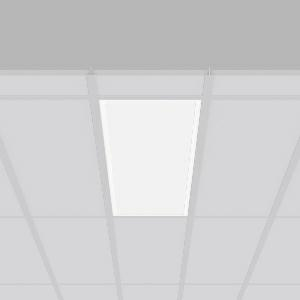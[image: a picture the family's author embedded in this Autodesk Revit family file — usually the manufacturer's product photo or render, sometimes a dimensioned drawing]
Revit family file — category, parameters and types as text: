
# Revit family: sidelite_eco_672372_002_04_a6ed
name_source: partatom
category: Lighting Fixtures
units: mm (PartAtom-declared; Revit-internal decimal feet)

## family parameters
Cut with Voids When Loaded = No
Host = Face
Light Source = No
Part Type = Normal
Room Calculation Point = No
Round Connector Dimension = Use Diameter
Shared = No

## types (1)
- SIDELITE ECO (1 x LED Modul 830, 3300 lm, 3000)
    Apparent Load = 29 VA
    CIE Flux Codes = 46 79 96 100 100
    Color Rendering = 80
    Color Temperature = 3000
    Default Elevation = 1800 mm
    Description = Series: SIDELITE ECO
Highly economical recessed luminaire with progressive LED technology. For escape route illumination. Frame made of aluminium, powder-coated. Diffuser: plastic, opal. Lightguide and diffuser made of non-yellowing plastic (PMMA). Lateral light emission (RZB SIDELITE technology) for homogeneous light distribution. External driver. Self-contained system with automatic self-test and feedback to the RZB monitoring system MULTIDIGIT. External driver with simple plug-in locking system. Extended connection cable (1.90 m). 
Colour: white
Length: 1195 mm
Width: 295 mm
Cut-out length: 1170 mm
Cut-out width: 270 mm
Recess height: 160 mm
Luminaire: recess height: 40 mm
Weight: 4.4 kg
Operating mode: maintained power mode
Duration time: 8 h
Lamp: LED
Socket: without socket
Colour temperature: 3000K
Colour rendering index (CRI): 80
System power: 29 W
Rated luminous flux: 3300 lm
Luminous flux, emergency: 220 lm
System power, emergency: 0.1 W
Control gear: Regulated power supply
Protection class: I
Type of protection: IP 40
    Height = 0 mm  [stored 0 ft]
    Lamp = 1 x LED Modul 830
    Lamp Light Flux = 3300 lm
    Lamp count = 1
    Length = 1195 mm
    Lifetime = 50000 h
    Luminous efficacy = 114 lm/W
    Manufacturer = RZB
    ModVariant = No
    Model = 672372.002.04
    Mounting Place = Ceiling
    Mounting Type = Recessed
    Number of Poles = 1
    OnlyDefault = Yes
    Power Factor = 1
    Product Name = SIDELITE ECO
    Product group = Recessed modular luminaires
    ProductGroupID = 406
    Protection Class = Protection class I
    Protection Degree = IP 40
    RLX_Detail_Level = 1
    RLX_Emergency_Light_Flux = 220 lm
    RLX_Emergency_Type = 3
    RLX_Emergency_Type_DB = Yes
    RlxData = <blob elided: 30697 chars, md5=66cfd266>
    Socket = socket
    Standby Power = 0 W
    System Light Flux = 3300 lm
    System Power = 29 W
    Type Comments = Product without accessories
    Type Image = 312365.002.jpg
    URL = http://relux.com
    VarID = ---
    Voltage = 230 V
    Voltage Range = 220-240 V
    Weight = 0.00 kg
    Width = 295 mm

note: [stored X ft] marks values corroborated as IEEE doubles in the binary element streams (Revit-internal decimal feet)

## geometry (parser evidence)
native form markers: Blend x4, Sweep x10
no freeform markers — native parametric forms only
